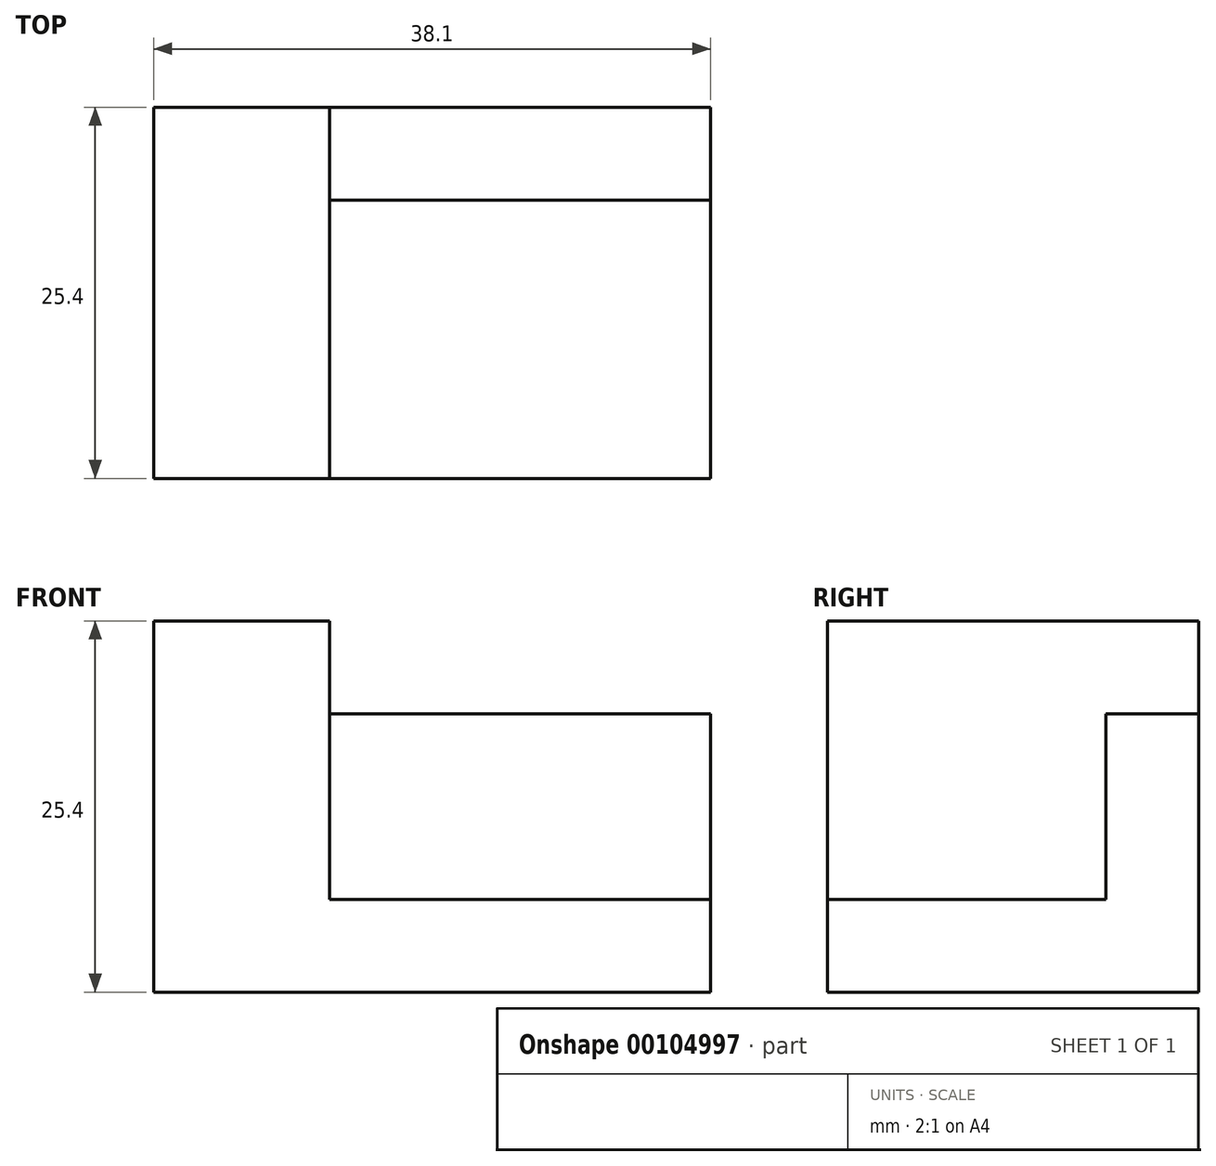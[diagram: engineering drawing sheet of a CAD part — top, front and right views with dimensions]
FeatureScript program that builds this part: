
annotation { "Feature Type Name" : "Feature", "Feature Type Description" : "" }
export const myFeature = defineFeature(function(context is Context, id is Id, definition is map)
    precondition{}
    {
        {
            var Q0;
            Q0=qCreatedBy(makeId("Front.planeOp"),FACE);
            var sketch = newSketch(context, id + "F0", { "sketchPlane" : qUnion([Q0])});
            skLineSegment(sketch, "E0.bottom", {"start": v(0, 0) * mm, "end": v(38.1, 0) * mm});
            skLineSegment(sketch, "E0.top", {"start": v(0, 25.4) * mm, "end": v(12.03, 25.4) * mm});
            skLineSegment(sketch, "E0.left", {"start": v(0, 0) * mm, "end": v(0, 25.4) * mm});
            skLineSegment(sketch, "E0.right", {"start": v(38.1, 0) * mm, "end": v(38.1, 19.05) * mm});
            skLineSegment(sketch, "E1.bottom", {"start": v(38.1, 19.05) * mm, "end": v(12.03, 19.05) * mm});
            skLineSegment(sketch, "E1.top", {"start": v(38.1, 6.35) * mm, "end": v(12.03, 6.35) * mm});
            skLineSegment(sketch, "E1.left", {"start": v(38.1, 19.05) * mm, "end": v(38.1, 6.35) * mm});
            skLineSegment(sketch, "E1.right", {"start": v(12.03, 19.05) * mm, "end": v(12.03, 6.35) * mm});
            skLineSegment(sketch, "E2", {"start": v(12.03, 19.05) * mm, "end": v(12.03, 25.4) * mm});
            skSolve(sketch);
        }
        {
            var Q0;
            Q0=makeQuery(id+"F0.imprint","IMPRINT",FACE,{"disambiguationData":[TD([[makeQuery(id+"F0.imprint","IMPRINT",EDGE,{"derivedFrom":sQuery(id+"F0.wireOp",EDGE,"E0.bottom")}),1.0]])]});
            extrude(context, id + "F1", {"entities" : qUnion([Q0]), "depth" : 25.4 * mm});
        }
        {
            var Q0;
            Q0=makeQuery(id+"F0.imprint","IMPRINT",FACE,{"disambiguationData":[TD([[makeQuery(id+"F0.imprint","IMPRINT",EDGE,{"derivedFrom":sQuery(id+"F0.wireOp",EDGE,"E1.bottom")}),1.0]])]});
            extrude(context, id + "F2", {"entities" : qUnion([Q0]), "operationType" : NewBodyOperationType.ADD, "depth" : 6.35 * mm});
        }
    });
